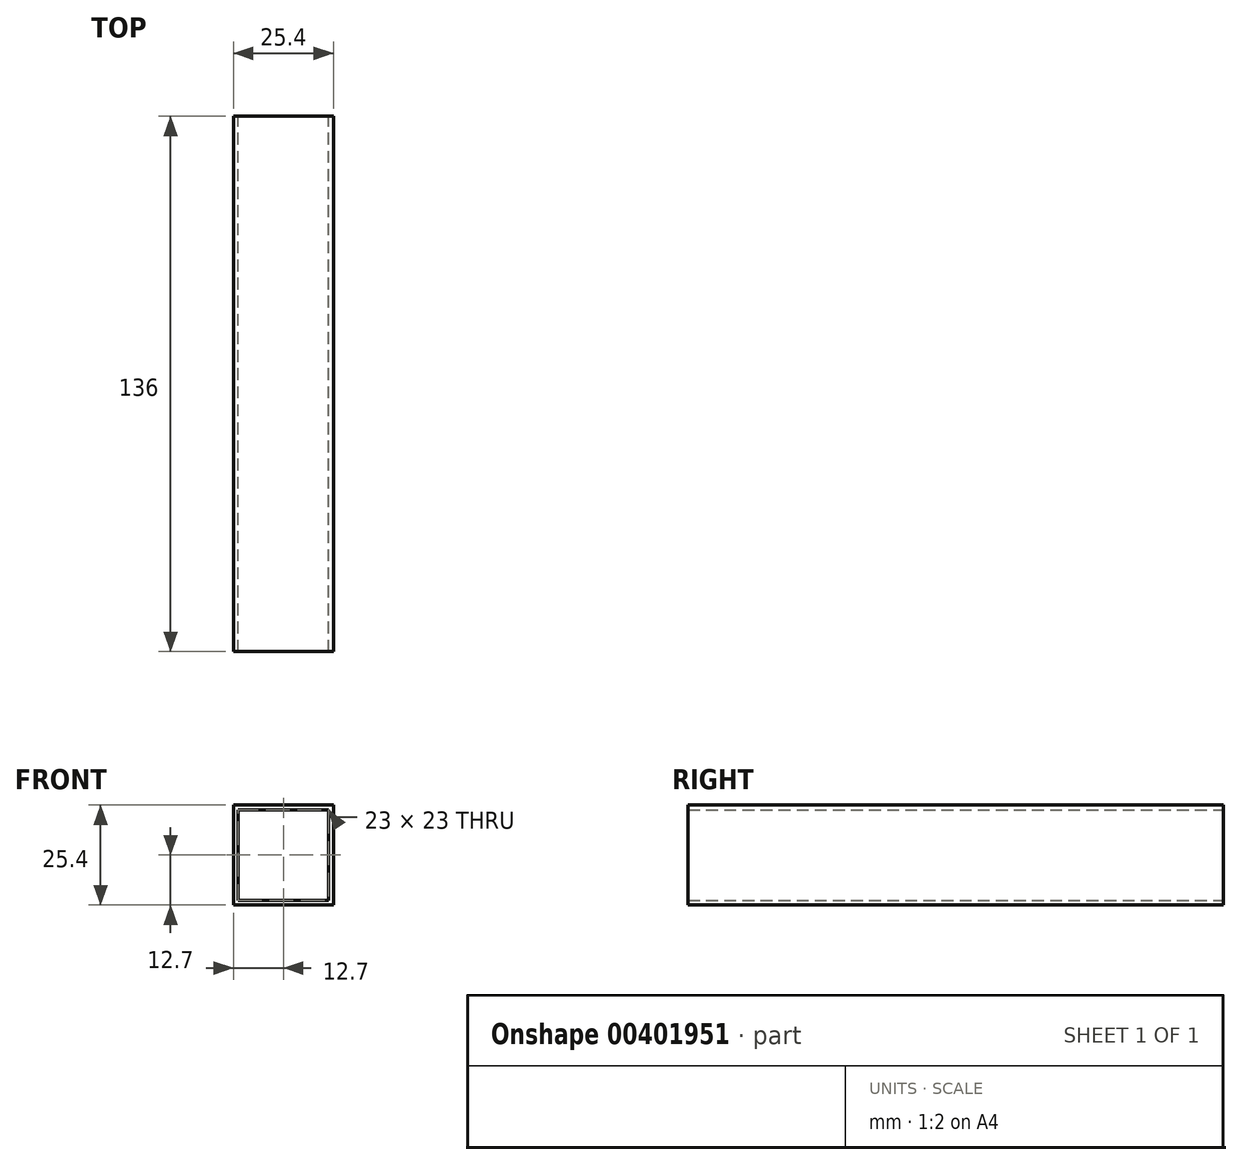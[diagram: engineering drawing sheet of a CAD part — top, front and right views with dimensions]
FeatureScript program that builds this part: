
annotation { "Feature Type Name" : "Feature", "Feature Type Description" : "" }
export const myFeature = defineFeature(function(context is Context, id is Id, definition is map)
    precondition{}
    {
        {
            var Q0;
            Q0=qCreatedBy(makeId("Front.planeOp"),FACE);
            var sketch = newSketch(context, id + "F0", { "sketchPlane" : qUnion([Q0])});
            skLineSegment(sketch, "E0.bottom", {"start": v(-12.7, 12.7) * mm, "end": v(12.7, 12.7) * mm});
            skLineSegment(sketch, "E0.top", {"start": v(-12.7, -12.7) * mm, "end": v(12.7, -12.7) * mm});
            skLineSegment(sketch, "E0.left", {"start": v(-12.7, 12.7) * mm, "end": v(-12.7, -12.7) * mm});
            skLineSegment(sketch, "E0.right", {"start": v(12.7, 12.7) * mm, "end": v(12.7, -12.7) * mm});
            skLineSegment(sketch, "E1", {"start": v(0, 0) * mm, "end": v(0, 12.7) * mm, "construction": true});
            skLineSegment(sketch, "E2", {"start": v(0, 0) * mm, "end": v(-12.7, 0) * mm, "construction": true});
            skLineSegment(sketch, "E3.0", {"start": v(-11.5, -11.5) * mm, "end": v(11.5, -11.5) * mm});
            skLineSegment(sketch, "E3.1", {"start": v(-11.5, 11.5) * mm, "end": v(-11.5, -11.5) * mm});
            skLineSegment(sketch, "E3.2", {"start": v(-11.5, 11.5) * mm, "end": v(11.5, 11.5) * mm});
            skLineSegment(sketch, "E3.3", {"start": v(11.5, 11.5) * mm, "end": v(11.5, -11.5) * mm});
            skSolve(sketch);
        }
        {
            var Q0;
            Q0=qSketchRegion(id+"F0",true);
            var Q1;
            Q1=qConstructionFilter(qBodyType(qCreatedBy(id+"F0",EDGE),BodyType.WIRE),ConstructionObject.NO);
            extrude(context, id + "F1", {"entities" : qUnion([Q0]), "surfaceEntities" : qUnion([Q1]), "endBound" : BoundingType.SYMMETRIC, "depth" : (200 - 45 - 19) * mm});
        }
    });
